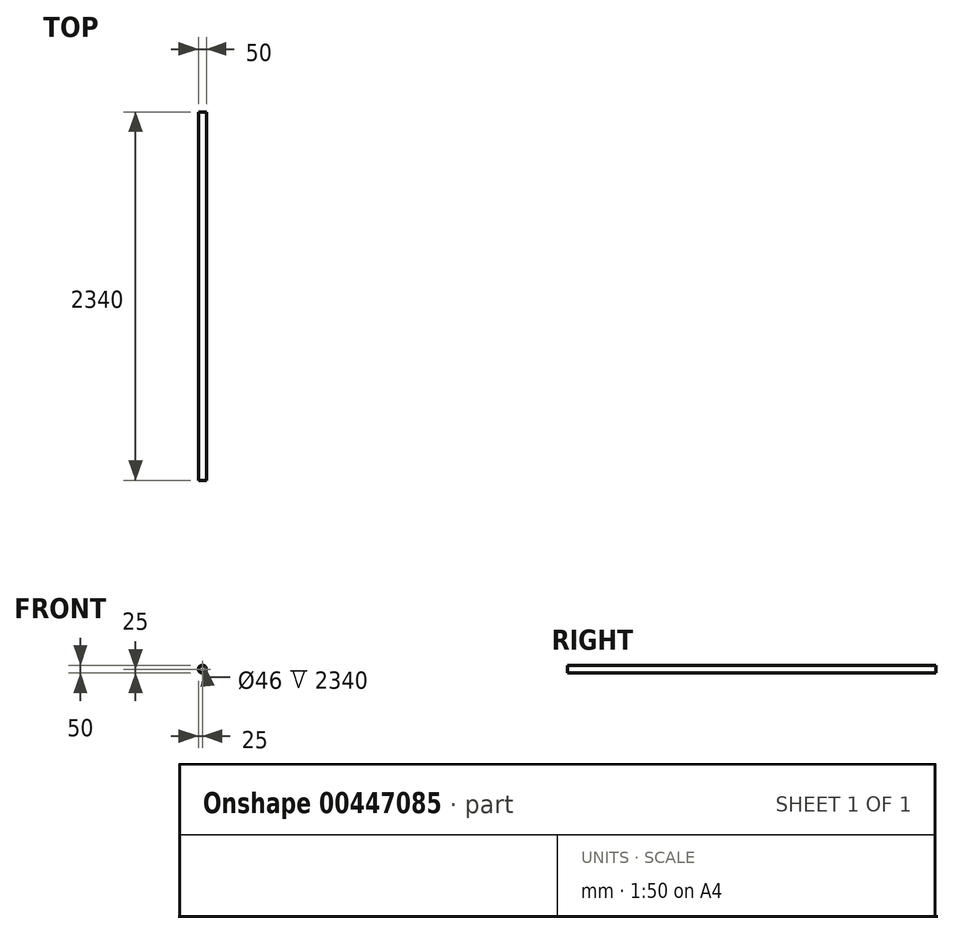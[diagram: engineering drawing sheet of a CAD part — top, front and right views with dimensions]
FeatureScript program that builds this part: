
annotation { "Feature Type Name" : "Feature", "Feature Type Description" : "" }
export const myFeature = defineFeature(function(context is Context, id is Id, definition is map)
    precondition{}
    {
        {
            var Q0;
            Q0=qCreatedBy(makeId("Front.planeOp"),FACE);
            var sketch = newSketch(context, id + "F0", { "sketchPlane" : qUnion([Q0])});
            skCircle(sketch, "E0", {"center": v(0, 0) * mm, "radius": 25 * mm});
            skCircle(sketch, "E1", {"center": v(0, 0) * mm, "radius": 23 * mm});
            skSolve(sketch);
        }
        {
            var Q0;
            Q0=makeQuery(id+"F0.imprint","IMPRINT",FACE,{"disambiguationData":[TD([[makeQuery(id+"F0.imprint","IMPRINT",EDGE,{"derivedFrom":sQuery(id+"F0.wireOp",EDGE,"E0")}),1.0]])]});
            extrude(context, id + "F1", {"entities" : qUnion([Q0]), "endBound" : BoundingType.SYMMETRIC, "depth" : 2340 * mm});
        }
    });
